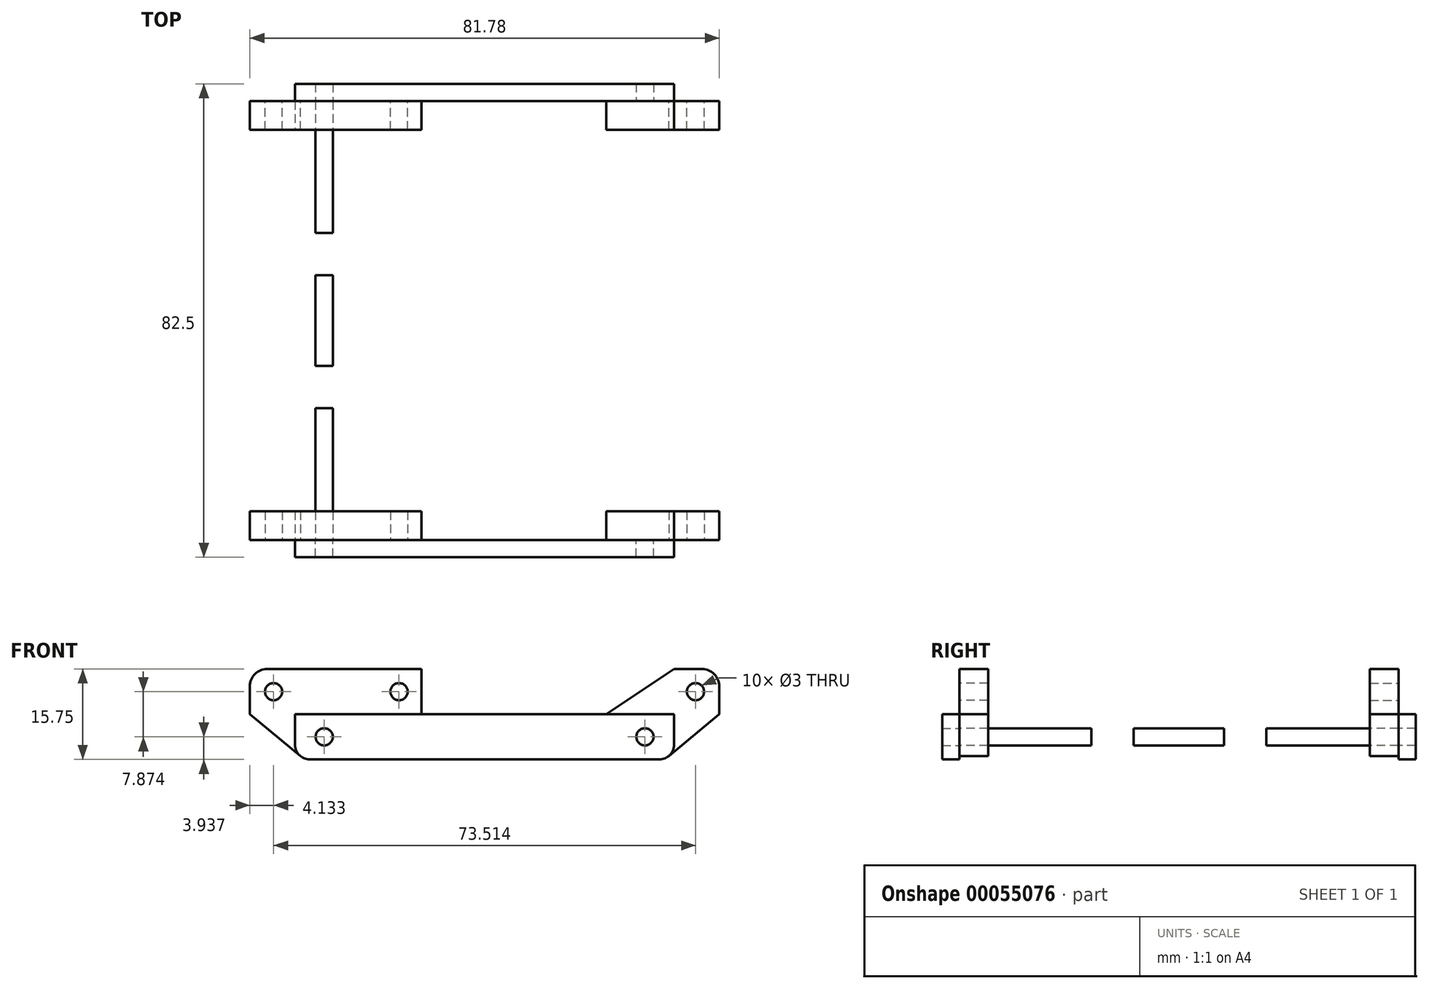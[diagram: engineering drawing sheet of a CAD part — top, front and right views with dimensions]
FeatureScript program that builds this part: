
annotation { "Feature Type Name" : "Feature", "Feature Type Description" : "" }
export const myFeature = defineFeature(function(context is Context, id is Id, definition is map)
    precondition{}
    {
        {
            var Q0;
            Q0=qCreatedBy(makeId("Top.planeOp"),FACE);
            var sketch = newSketch(context, id + "F0", { "sketchPlane" : qUnion([Q0])});
            skLineSegment(sketch, "E0", {"start": v(0, -38.25) * mm, "end": v(33.02, -38.25) * mm});
            skLineSegment(sketch, "E1", {"start": v(33.02, -38.25) * mm, "end": v(33.02, -15.25) * mm});
            skLineSegment(sketch, "E2", {"start": v(33.02, -15.25) * mm, "end": v(20.32, -15.25) * mm});
            skLineSegment(sketch, "E3", {"start": v(20.32, -15.25) * mm, "end": v(20.32, -7.88) * mm});
            skLineSegment(sketch, "E4", {"start": v(20.32, -7.88) * mm, "end": v(33.02, -7.88) * mm});
            skLineSegment(sketch, "E5", {"start": v(33.02, -7.88) * mm, "end": v(33.02, 0) * mm});
            skLineSegment(sketch, "E6.MirrorCS", {"start": v(0, 38.25) * mm, "end": v(33.02, 38.25) * mm});
            skLineSegment(sketch, "E7.MirrorCS", {"start": v(33.02, 38.25) * mm, "end": v(33.02, 15.25) * mm});
            skLineSegment(sketch, "E8.MirrorCS", {"start": v(33.02, 15.25) * mm, "end": v(20.32, 15.25) * mm});
            skLineSegment(sketch, "E9.MirrorCS", {"start": v(20.32, 15.25) * mm, "end": v(20.32, 7.88) * mm});
            skLineSegment(sketch, "E10.MirrorCS", {"start": v(20.32, 7.88) * mm, "end": v(33.02, 7.88) * mm});
            skLineSegment(sketch, "E11.MirrorCS", {"start": v(33.02, 7.88) * mm, "end": v(33.02, 0) * mm});
            skLineSegment(sketch, "E12.MirrorCS", {"start": v(0, -38.25) * mm, "end": v(-33.02, -38.25) * mm});
            skLineSegment(sketch, "E13.MirrorCS", {"start": v(-33.02, -38.25) * mm, "end": v(-33.02, -15.25) * mm});
            skLineSegment(sketch, "E14.MirrorCS", {"start": v(-33.02, -15.25) * mm, "end": v(-20.32, -15.25) * mm});
            skLineSegment(sketch, "E15.MirrorCS", {"start": v(-20.32, -15.25) * mm, "end": v(-20.32, -7.88) * mm});
            skLineSegment(sketch, "E16.MirrorCS", {"start": v(-20.32, -7.88) * mm, "end": v(-33.02, -7.88) * mm});
            skLineSegment(sketch, "E17.MirrorCS", {"start": v(-33.02, -7.88) * mm, "end": v(-33.02, 0) * mm});
            skLineSegment(sketch, "E18.MirrorCS", {"start": v(-33.02, 7.88) * mm, "end": v(-33.02, 0) * mm});
            skLineSegment(sketch, "E19.MirrorCS", {"start": v(-20.32, 7.88) * mm, "end": v(-33.02, 7.88) * mm});
            skLineSegment(sketch, "E20.MirrorCS", {"start": v(-20.32, 15.25) * mm, "end": v(-20.32, 7.88) * mm});
            skLineSegment(sketch, "E21.MirrorCS", {"start": v(-33.02, 15.25) * mm, "end": v(-20.32, 15.25) * mm});
            skLineSegment(sketch, "E22.MirrorCS", {"start": v(-33.02, 38.25) * mm, "end": v(-33.02, 15.25) * mm});
            skLineSegment(sketch, "E23.MirrorCS", {"start": v(0, 38.25) * mm, "end": v(-33.02, 38.25) * mm});
            skCircle(sketch, "E24", {"center": v(14.02, 30.31) * mm, "radius": 1.5 * mm});
            skCircle(sketch, "E25", {"center": v(11.6, 8.09) * mm, "radius": 1.5 * mm});
            skLineSegment(sketch, "E26", {"start": v(6.02, 38.25) * mm, "end": v(6.02, -38.25) * mm, "construction": true});
            skCircle(sketch, "E27.MirrorC", {"center": v(-1.98, 30.31) * mm, "radius": 1.5 * mm});
            skCircle(sketch, "E28.MirrorC", {"center": v(0.43, 8.09) * mm, "radius": 1.5 * mm});
            skLineSegment(sketch, "E29", {"start": v(0, 0) * mm, "end": v(33.02, 0) * mm, "construction": true});
            skSolve(sketch);
        }
        {
            var Q0;
            Q0=makeQuery(id+"F0.imprint","IMPRINT",FACE,{"disambiguationData":[TD([[makeQuery(id+"F0.imprint","IMPRINT",EDGE,{"derivedFrom":sQuery(id+"F0.wireOp",EDGE,"E28.MirrorC")}),1.0]])]});
            var Q1;
            Q1=makeQuery(id+"F0.imprint","IMPRINT",FACE,{"disambiguationData":[TD([[makeQuery(id+"F0.imprint","IMPRINT",EDGE,{"derivedFrom":sQuery(id+"F0.wireOp",EDGE,"E25")}),-1.0]])]});
            var Q2;
            Q2=makeQuery(id+"F0.imprint","IMPRINT",FACE,{"disambiguationData":[TD([[makeQuery(id+"F0.imprint","IMPRINT",EDGE,{"derivedFrom":sQuery(id+"F0.wireOp",EDGE,"E27.MirrorC")}),1.0]])]});
            var Q3;
            Q3=makeQuery(id+"F0.imprint","IMPRINT",FACE,{"disambiguationData":[TD([[makeQuery(id+"F0.imprint","IMPRINT",EDGE,{"derivedFrom":sQuery(id+"F0.wireOp",EDGE,"E24")}),-1.0]])]});
            var Q4;
            {var subQ3=sQuery(id+"F0.wireOp",EDGE,"9118c8c8-0fbe-4123-afdf-e2b0a5df1f7e");Q4=makeQuery(id+"F0.imprint","IMPRINT",FACE,{"disambiguationData":[TD([[makeQuery(id+"F0.imprint","IMPRINT",EDGE,{"derivedFrom":subQ3}),-1.0]])]});}
            var Q5;
            Q5=makeQuery(id+"F0.imprint","IMPRINT",FACE,{"disambiguationData":[TD([[makeQuery(id+"F0.imprint","IMPRINT",EDGE,{"derivedFrom":sQuery(id+"F0.wireOp",EDGE,"2c91735e-b4bf-4d13-a7d5-686ce264821d")}),1.0]])]});
            var Q6;
            {var subQ0=sQuery(id+"F0.wireOp",EDGE,"2e4b5a47-8200-4868-9fea-fa7b647ed2cf");Q6=makeQuery(id+"F0.imprint","IMPRINT",FACE,{"disambiguationData":[TD([[makeQuery(id+"F0.imprint","IMPRINT",EDGE,{"derivedFrom":subQ0}),-1.0]])]});}
            var Q7;
            Q7=makeQuery(id+"F0.imprint","IMPRINT",FACE,{"disambiguationData":[TD([[makeQuery(id+"F0.imprint","IMPRINT",EDGE,{"derivedFrom":sQuery(id+"F0.wireOp",EDGE,"E0")}),1.0]])]});
            extrude(context, id + "F1", {"entities" : qUnion([Q0, Q1, Q2, Q3, Q4, Q5, Q6, Q7]), "depth" : 7.87 * mm});
        }
        {
            var Q0;
            Q0=makeQuery(id+"F1.opExtrude","SWEPT_EDGE",EDGE,{"disambiguationData":[OSD([sQuery(id+"F0.wireOp",EDGE,"E3"),sQuery(id+"F0.wireOp",EDGE,"E4")])]});
            var Q1;
            Q1=makeQuery(id+"F1.opExtrude","SWEPT_EDGE",EDGE,{"disambiguationData":[OSD([sQuery(id+"F0.wireOp",EDGE,"E2"),sQuery(id+"F0.wireOp",EDGE,"E3")])]});
            var Q2;
            Q2=makeQuery(id+"F1.opExtrude","SWEPT_EDGE",EDGE,{"disambiguationData":[OSD([sQuery(id+"F0.wireOp",EDGE,"E9.MirrorCS"),sQuery(id+"F0.wireOp",EDGE,"E10.MirrorCS")])]});
            var Q3;
            Q3=makeQuery(id+"F1.opExtrude","SWEPT_EDGE",EDGE,{"disambiguationData":[OSD([sQuery(id+"F0.wireOp",EDGE,"E8.MirrorCS"),sQuery(id+"F0.wireOp",EDGE,"E9.MirrorCS")])]});
            var Q4;
            Q4=makeQuery(id+"F1.opExtrude","SWEPT_EDGE",EDGE,{"disambiguationData":[OSD([sQuery(id+"F0.wireOp",EDGE,"E15.MirrorCS"),sQuery(id+"F0.wireOp",EDGE,"E16.MirrorCS")])]});
            var Q5;
            Q5=makeQuery(id+"F1.opExtrude","SWEPT_EDGE",EDGE,{"disambiguationData":[OSD([sQuery(id+"F0.wireOp",EDGE,"E20.MirrorCS"),sQuery(id+"F0.wireOp",EDGE,"E21.MirrorCS")])]});
            var Q6;
            Q6=makeQuery(id+"F1.opExtrude","SWEPT_EDGE",EDGE,{"disambiguationData":[OSD([sQuery(id+"F0.wireOp",EDGE,"E19.MirrorCS"),sQuery(id+"F0.wireOp",EDGE,"E20.MirrorCS")])]});
            var Q7;
            Q7=makeQuery(id+"F1.opExtrude","SWEPT_EDGE",EDGE,{"disambiguationData":[OSD([sQuery(id+"F0.wireOp",EDGE,"E14.MirrorCS"),sQuery(id+"F0.wireOp",EDGE,"E15.MirrorCS")])]});
            var Q8;
            Q8=makeQuery(id+"F1.opExtrude","CAP_EDGE",EDGE,{"disambiguationData":[OSD([sQuery(id+"F0.wireOp",EDGE,"E1")])],"isStart":true});
            var Q9;
            Q9=makeQuery(id+"F1.opExtrude","CAP_EDGE",EDGE,{"disambiguationData":[OSD([sQuery(id+"F0.wireOp",EDGE,"E5"),sQuery(id+"F0.wireOp",EDGE,"E11.MirrorCS")])],"isStart":true});
            var Q10;
            Q10=makeQuery(id+"F1.opExtrude","CAP_EDGE",EDGE,{"disambiguationData":[OSD([sQuery(id+"F0.wireOp",EDGE,"E7.MirrorCS")])],"isStart":true});
            var Q11;
            Q11=makeQuery(id+"F1.opExtrude","CAP_EDGE",EDGE,{"disambiguationData":[OSD([sQuery(id+"F0.wireOp",EDGE,"E22.MirrorCS")])],"isStart":true});
            var Q12;
            Q12=makeQuery(id+"F1.opExtrude","CAP_EDGE",EDGE,{"disambiguationData":[OSD([sQuery(id+"F0.wireOp",EDGE,"E17.MirrorCS"),sQuery(id+"F0.wireOp",EDGE,"E18.MirrorCS")])],"isStart":true});
            var Q13;
            Q13=makeQuery(id+"F1.opExtrude","CAP_EDGE",EDGE,{"disambiguationData":[OSD([sQuery(id+"F0.wireOp",EDGE,"E13.MirrorCS")])],"isStart":true});
            fillet(context, id + "F2", {"entities" : qUnion([Q0, Q1, Q2, Q3, Q4, Q5, Q6, Q7, Q8, Q9, Q10, Q11, Q12, Q13]), "radius" : 2.54 * mm, "tangentPropagation" : true, "allowEdgeOverflow" : false});
        }
        {
            var Q0;
            Q0=sQuery(id+"F0.wireOp",VERTEX,"E28.MirrorC.center");
            var Q1;
            Q1=sQuery(id+"F0.wireOp",VERTEX,"E25.center");
            var Q2;
            Q2=sQuery(id+"F0.wireOp",VERTEX,"E24.center");
            var Q3;
            Q3=sQuery(id+"F0.wireOp",VERTEX,"E27.MirrorC.center");
            var Q4;
            Q4=makeQuery(id+"F1.opExtrude","SWEPT_BODY",BODY,{"disambiguationData":[OSD([sQuery(id+"F0.wireOp",EDGE,"E0"),sQuery(id+"F0.wireOp",EDGE,"E1"),sQuery(id+"F0.wireOp",EDGE,"E2"),sQuery(id+"F0.wireOp",EDGE,"E3"),sQuery(id+"F0.wireOp",EDGE,"E4"),sQuery(id+"F0.wireOp",EDGE,"E5"),sQuery(id+"F0.wireOp",EDGE,"E6.MirrorCS"),sQuery(id+"F0.wireOp",EDGE,"E7.MirrorCS"),sQuery(id+"F0.wireOp",EDGE,"E8.MirrorCS"),sQuery(id+"F0.wireOp",EDGE,"E9.MirrorCS"),sQuery(id+"F0.wireOp",EDGE,"E10.MirrorCS"),sQuery(id+"F0.wireOp",EDGE,"E11.MirrorCS"),sQuery(id+"F0.wireOp",EDGE,"E12.MirrorCS"),sQuery(id+"F0.wireOp",EDGE,"E13.MirrorCS"),sQuery(id+"F0.wireOp",EDGE,"E14.MirrorCS"),sQuery(id+"F0.wireOp",EDGE,"E15.MirrorCS"),sQuery(id+"F0.wireOp",EDGE,"E16.MirrorCS"),sQuery(id+"F0.wireOp",EDGE,"E17.MirrorCS"),sQuery(id+"F0.wireOp",EDGE,"E18.MirrorCS"),sQuery(id+"F0.wireOp",EDGE,"E19.MirrorCS"),sQuery(id+"F0.wireOp",EDGE,"E20.MirrorCS"),sQuery(id+"F0.wireOp",EDGE,"E21.MirrorCS"),sQuery(id+"F0.wireOp",EDGE,"E22.MirrorCS"),sQuery(id+"F0.wireOp",EDGE,"E23.MirrorCS"),sQuery(id+"F0.wireOp",EDGE,"E24"),sQuery(id+"F0.wireOp",EDGE,"E25"),sQuery(id+"F0.wireOp",EDGE,"E27.MirrorC"),sQuery(id+"F0.wireOp",EDGE,"E28.MirrorC")])]});
            hole(context, id + "F3", {"style" : HoleStyle.C_SINK, "holeDiameter" : 3.5 * mm, "cSinkDiameter" : 6 * mm, "endStyle" : HoleEndStyle.BLIND, "oppositeDirection" : true, "holeDepth" : 10 * mm, "locations" : qUnion([Q0, Q1, Q2, Q3]), "scope" : qUnion([Q4]), "cSinkAngle" : 90 * degree});
        }
        {
            var Q0;
            Q0=makeQuery(id+"F1.opExtrude","SWEPT_FACE",FACE,{"disambiguationData":[OSD([sQuery(id+"F0.wireOp",EDGE,"E0"),sQuery(id+"F0.wireOp",EDGE,"E12.MirrorCS")])]});
            var sketch = newSketch(context, id + "F4", { "sketchPlane" : qUnion([Q0])});
            skCircle(sketch, "E30", {"center": v(27.94, 3.94) * mm, "radius": 1.5 * mm});
            skLineSegment(sketch, "E31", {"start": v(23.1, 3.94) * mm, "end": v(27.94, 3.94) * mm, "construction": true});
            skCircle(sketch, "E32.MirrorC", {"center": v(-27.94, 3.94) * mm, "radius": 1.5 * mm});
            skLineSegment(sketch, "E33", {"start": v(33.02, 15.75) * mm, "end": v(40.9, 15.75) * mm});
            skLineSegment(sketch, "E34", {"start": v(40.9, 15.75) * mm, "end": v(40.9, 7.87) * mm});
            skCircle(sketch, "E35", {"center": v(36.76, 11.81) * mm, "radius": 1.5 * mm});
            skLineSegment(sketch, "E36", {"start": v(27.94, 3.94) * mm, "end": v(27.94, 0) * mm, "construction": true});
            skLineSegment(sketch, "E37", {"start": v(36.76, 11.81) * mm, "end": v(36.76, 15.75) * mm, "construction": true});
            skLineSegment(sketch, "E38", {"start": v(0, 7.87) * mm, "end": v(0, 0) * mm, "construction": true});
            skLineSegment(sketch, "E39", {"start": v(33.02, 7.87) * mm, "end": v(33.02, 15.75) * mm, "construction": true});
            skLineSegment(sketch, "E40", {"start": v(32.1, 0.58) * mm, "end": v(40.9, 7.87) * mm});
            skLineSegment(sketch, "E41", {"start": v(21.2, 7.87) * mm, "end": v(25.15, 7.87) * mm, "construction": true});
            skLineSegment(sketch, "E42", {"start": v(25.15, 7.87) * mm, "end": v(33.02, 7.87) * mm, "construction": true});
            skLineSegment(sketch, "E43.MirrorCS", {"start": v(-21.2, 7.87) * mm, "end": v(-33.02, 15.75) * mm});
            skLineSegment(sketch, "E44.MirrorCS", {"start": v(-33.02, 15.75) * mm, "end": v(-40.9, 15.75) * mm});
            skLineSegment(sketch, "E45.MirrorCS", {"start": v(-40.9, 15.75) * mm, "end": v(-40.9, 7.87) * mm});
            skCircle(sketch, "E46.MirrorC", {"center": v(-36.76, 11.81) * mm, "radius": 1.5 * mm});
            skLineSegment(sketch, "E47.MirrorCS", {"start": v(-32.1, 0.58) * mm, "end": v(-40.9, 7.87) * mm});
            skLineSegment(sketch, "E48", {"start": v(14.9, 11.81) * mm, "end": v(14.9, 7.87) * mm, "construction": true});
            skLineSegment(sketch, "E49", {"start": v(21.2, 7.87) * mm, "end": v(33.02, 15.75) * mm});
            skLineSegment(sketch, "E50", {"start": v(-33.02, 15.75) * mm, "end": v(-10.96, 15.75) * mm});
            skLineSegment(sketch, "E51", {"start": v(-10.96, 15.75) * mm, "end": v(-10.96, 7.87) * mm});
            skCircle(sketch, "E52", {"center": v(-14.9, 11.81) * mm, "radius": 1.5 * mm});
            skLineSegment(sketch, "E53", {"start": v(-14.9, 11.81) * mm, "end": v(-14.9, 15.75) * mm, "construction": true});
            skLineSegment(sketch, "E54", {"start": v(-14.9, 15.75) * mm, "end": v(-14.9, 11.81) * mm, "construction": true});
            skLineSegment(sketch, "E55", {"start": v(-10.96, 11.81) * mm, "end": v(-14.9, 11.81) * mm, "construction": true});
            skSolve(sketch);
        }
        {
            var Q0;
            {var subQ0=sQuery(id+"F4.wireOp",EDGE,"E43.MirrorCS");Q0=makeQuery(id+"F4.imprint","IMPRINT",FACE,{"disambiguationData":[TD([[makeQuery(id+"F4.imprint","IMPRINT",EDGE,{"derivedFrom":subQ0}),1.0]])]});}
            var Q1;
            {var subQ0=sQuery(id+"F4.wireOp",EDGE,"E43.MirrorCS");Q1=makeQuery(id+"F4.imprint","IMPRINT",FACE,{"disambiguationData":[TD([[makeQuery(id+"F4.imprint","IMPRINT",EDGE,{"derivedFrom":subQ0}),-1.0]])]});}
            var Q2;
            Q2=makeQuery(id+"F4.imprint","IMPRINT",FACE,{"disambiguationData":[TD([[makeQuery(id+"F4.imprint","IMPRINT",EDGE,{"derivedFrom":sQuery(id+"F4.wireOp",EDGE,"E33")}),-1.0]])]});
            extrude(context, id + "F5", {"entities" : qUnion([Q0, Q1, Q2]), "oppositeDirection" : true, "depth" : 5 * mm});
        }
        {
            var Q0;
            Q0=makeQuery(id+"F5.opExtrude","SWEPT_BODY",BODY,{"disambiguationData":[OSD([sQuery(id+"F0.wireOp",EDGE,"E0"),sQuery(id+"F0.wireOp",EDGE,"E12.MirrorCS"),sQuery(id+"F0.wireOp",EDGE,"E13.MirrorCS"),sQuery(id+"F4.wireOp",EDGE,"E44.MirrorCS"),sQuery(id+"F4.wireOp",EDGE,"E45.MirrorCS"),sQuery(id+"F4.wireOp",EDGE,"E46.MirrorC"),sQuery(id+"F4.wireOp",EDGE,"E47.MirrorCS"),sQuery(id+"F4.wireOp",EDGE,"E50"),sQuery(id+"F4.wireOp",EDGE,"E51"),sQuery(id+"F4.wireOp",EDGE,"E52")])]});
            var Q1;
            Q1=makeQuery(id+"F5.opExtrude","SWEPT_BODY",BODY,{"disambiguationData":[OSD([sQuery(id+"F0.wireOp",EDGE,"E0"),sQuery(id+"F0.wireOp",EDGE,"E1"),sQuery(id+"F0.wireOp",EDGE,"E12.MirrorCS"),sQuery(id+"F4.wireOp",EDGE,"E33"),sQuery(id+"F4.wireOp",EDGE,"E34"),sQuery(id+"F4.wireOp",EDGE,"E35"),sQuery(id+"F4.wireOp",EDGE,"E40"),sQuery(id+"F4.wireOp",EDGE,"E49")])]});
            var Q2;
            Q2=qCreatedBy(makeId("Front.planeOp"),FACE);
            mirror(context, id + "F6", {"operationType" : NewBodyOperationType.ADD, "entities" : qUnion([Q0, Q1]), "mirrorPlane" : qUnion([Q2])});
        }
        {
            var Q0;
            Q0=makeQuery(id+"F4.imprint","IMPRINT",FACE,{"disambiguationData":[TD([[makeQuery(id+"F4.imprint","IMPRINT",EDGE,{"derivedFrom":sQuery(id+"F4.wireOp",EDGE,"E32.MirrorC")}),-1.0]])]});
            var Q1;
            Q1=makeQuery(id+"F4.imprint","IMPRINT",FACE,{"disambiguationData":[TD([[makeQuery(id+"F4.imprint","IMPRINT",EDGE,{"derivedFrom":sQuery(id+"F4.wireOp",EDGE,"E30")}),1.0]])]});
            extrude(context, id + "F7", {"entities" : qUnion([Q0, Q1]), "operationType" : NewBodyOperationType.REMOVE, "endBound" : BoundingType.THROUGH_ALL, "oppositeDirection" : true, "depth" : 25 * mm});
        }
        {
            var Q0;
            Q0=makeQuery(id+"F4.imprint","IMPRINT",FACE,{"disambiguationData":[TD([[makeQuery(id+"F4.imprint","IMPRINT",EDGE,{"derivedFrom":sQuery(id+"F4.wireOp",EDGE,"E30")}),-1.0]])]});
            extrude(context, id + "F8", {"entities" : qUnion([Q0]), "depth" : 3 * mm});
        }
        {
            var Q0;
            Q0=makeQuery(id+"F8.opExtrude","SWEPT_BODY",BODY,{"disambiguationData":[OSD([sQuery(id+"F0.wireOp",EDGE,"E0"),sQuery(id+"F0.wireOp",EDGE,"E1"),sQuery(id+"F0.wireOp",EDGE,"E12.MirrorCS"),sQuery(id+"F0.wireOp",EDGE,"E13.MirrorCS"),sQuery(id+"F4.wireOp",EDGE,"E30"),sQuery(id+"F4.wireOp",EDGE,"E32.MirrorC")])]});
            var Q1;
            Q1=qCreatedBy(makeId("Front.planeOp"),FACE);
            mirror(context, id + "F9", {"operationType" : NewBodyOperationType.ADD, "entities" : qUnion([Q0]), "mirrorPlane" : qUnion([Q1])});
        }
        {
            var Q0;
            Q0=makeQuery(id+"F5.opExtrude","SWEPT_EDGE",EDGE,{"disambiguationData":[OSD([sQuery(id+"F4.wireOp",EDGE,"E44.MirrorCS"),sQuery(id+"F4.wireOp",EDGE,"E45.MirrorCS")])]});
            var Q1;
            Q1=makeQuery(id+"F6.opPattern","COPY",EDGE,{"derivedFrom":makeQuery(id+"F5.opExtrude","SWEPT_EDGE",EDGE,{"disambiguationData":[OSD([sQuery(id+"F4.wireOp",EDGE,"E33"),sQuery(id+"F4.wireOp",EDGE,"E34")])]}),"instanceName":"1"});
            var Q2;
            Q2=makeQuery(id+"F5.opExtrude","SWEPT_EDGE",EDGE,{"disambiguationData":[OSD([sQuery(id+"F4.wireOp",EDGE,"E33"),sQuery(id+"F4.wireOp",EDGE,"E34")])]});
            var Q3;
            Q3=makeQuery(id+"F6.opPattern","COPY",EDGE,{"derivedFrom":makeQuery(id+"F5.opExtrude","SWEPT_EDGE",EDGE,{"disambiguationData":[OSD([sQuery(id+"F4.wireOp",EDGE,"E44.MirrorCS"),sQuery(id+"F4.wireOp",EDGE,"E45.MirrorCS")])]}),"instanceName":"1"});
            fillet(context, id + "F10", {"entities" : qUnion([Q0, Q1, Q2, Q3]), "radius" : 3 * mm, "tangentPropagation" : true, "allowEdgeOverflow" : false});
        }
    });
